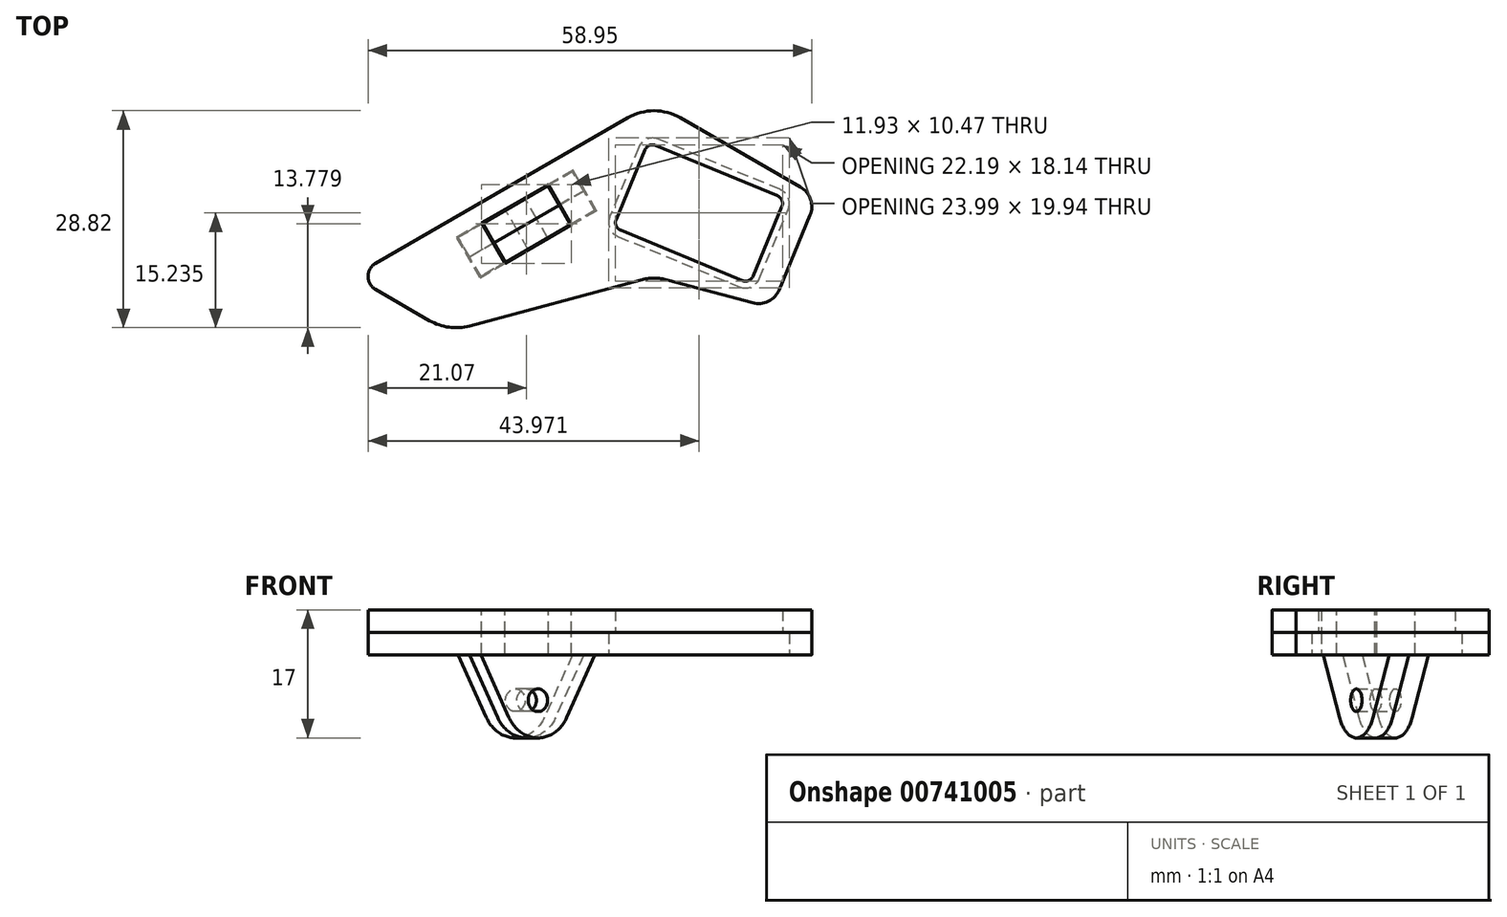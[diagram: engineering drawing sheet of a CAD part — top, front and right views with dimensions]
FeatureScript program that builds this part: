
annotation { "Feature Type Name" : "Feature", "Feature Type Description" : "" }
export const myFeature = defineFeature(function(context is Context, id is Id, definition is map)
    precondition{}
    {
        {
            var Q0;
            Q0=qCreatedBy(makeId("Top.planeOp"),FACE);
            var sketch = newSketch(context, id + "F0", { "sketchPlane" : qUnion([Q0])});
            skLineSegment(sketch, "E0", {"start": v(-37, 1.73) * mm, "end": v(-3.5, 21.07) * mm});
            skLineSegment(sketch, "E1", {"start": v(40, 0) * mm, "end": v(21.73, 10.55) * mm, "construction": true});
            skLineSegment(sketch, "E2", {"start": v(-1.81, -0.49) * mm, "end": v(-24.52, -6.57) * mm});
            skLineSegment(sketch, "E3", {"start": v(0, 0) * mm, "end": v(0, 23.1) * mm, "construction": true});
            skLineSegment(sketch, "E4", {"start": v(40, 0) * mm, "end": v(27.32, -7.32) * mm, "construction": true});
            skLineSegment(sketch, "E5", {"start": v(-29.83, -5.87) * mm, "end": v(-40, 0) * mm});
            skLineSegment(sketch, "E6", {"start": v(27.32, -7.32) * mm, "end": v(0, -23.1) * mm, "construction": true});
            skLineSegment(sketch, "E7", {"start": v(0, -23.1) * mm, "end": v(-37, -1.73) * mm, "construction": true});
            skLineSegment(sketch, "E8", {"start": v(13.99, -0.3) * mm, "end": v(17.82, 8.93) * mm});
            skLineSegment(sketch, "E9", {"start": v(16.73, 11.54) * mm, "end": v(0.57, 18.24) * mm});
            skLineSegment(sketch, "E10", {"start": v(-2.05, 17.16) * mm, "end": v(-5.87, 7.92) * mm});
            skLineSegment(sketch, "E11", {"start": v(-4.8, 5.3) * mm, "end": v(11.38, -1.4) * mm});
            skPoint(sketch, "E12.visualSharp", {"position": v(-6.64, 6.07) * mm});
            skArc(sketch, "E12.filletArc", {"start": v(-5.87, 7.92) * mm, "mid": v(-5.87, 6.39) * mm, "end": v(-4.8, 5.3) * mm});
            skPoint(sketch, "E13.visualSharp", {"position": v(-1.28, 19) * mm});
            skArc(sketch, "E13.filletArc", {"start": v(0.57, 18.24) * mm, "mid": v(-0.96, 18.24) * mm, "end": v(-2.05, 17.16) * mm});
            skPoint(sketch, "E14.visualSharp", {"position": v(18.58, 10.78) * mm});
            skArc(sketch, "E14.filletArc", {"start": v(17.82, 8.93) * mm, "mid": v(17.82, 10.46) * mm, "end": v(16.73, 11.54) * mm});
            skPoint(sketch, "E15.visualSharp", {"position": v(13.22, -2.16) * mm});
            skArc(sketch, "E15.filletArc", {"start": v(11.38, -1.4) * mm, "mid": v(12.9, -1.4) * mm, "end": v(13.99, -0.3) * mm});
            skLineSegment(sketch, "E16", {"start": v(16.64, -1.76) * mm, "end": v(20.73, 8.12) * mm});
            skLineSegment(sketch, "E17", {"start": v(15.63, -4.19) * mm, "end": v(27.32, -7.32) * mm, "construction": true});
            skLineSegment(sketch, "E18", {"start": v(13.09, -3.5) * mm, "end": v(1.81, -0.49) * mm});
            skLineSegment(sketch, "E19", {"start": v(3.5, 21.07) * mm, "end": v(19.45, 11.86) * mm});
            skPoint(sketch, "E20.visualSharp", {"position": v(15.63, -4.19) * mm});
            skArc(sketch, "E20.filletArc", {"start": v(13.09, -3.5) * mm, "mid": v(15.2, -3.3) * mm, "end": v(16.64, -1.76) * mm});
            skPoint(sketch, "E21.visualSharp", {"position": v(21.73, 10.55) * mm});
            skArc(sketch, "E21.filletArc", {"start": v(20.73, 8.12) * mm, "mid": v(20.8, 10.23) * mm, "end": v(19.45, 11.86) * mm});
            skPoint(sketch, "E22.visualSharp", {"position": v(0, 0) * mm});
            skArc(sketch, "E22.filletArc", {"start": v(1.81, -0.49) * mm, "mid": v(0, -0.25) * mm, "end": v(-1.81, -0.49) * mm});
            skPoint(sketch, "E23.visualSharp", {"position": v(-27.32, -7.32) * mm});
            skArc(sketch, "E23.filletArc", {"start": v(-29.83, -5.87) * mm, "mid": v(-27.25, -6.75) * mm, "end": v(-24.52, -6.57) * mm});
            skPoint(sketch, "E24.visualSharp", {"position": v(0, 23.1) * mm});
            skArc(sketch, "E24.filletArc", {"start": v(3.5, 21.07) * mm, "mid": v(0, 22.01) * mm, "end": v(-3.5, 21.07) * mm});
            skPoint(sketch, "E25.visualSharp", {"position": v(-40, 0) * mm});
            skArc(sketch, "E25.filletArc", {"start": v(-37, 1.73) * mm, "mid": v(-38, 0) * mm, "end": v(-37, -1.73) * mm});
            skSolve(sketch);
        }
        {
            var Q0;
            Q0=makeQuery(id+"F0.imprint","IMPRINT",FACE,{"disambiguationData":[TD([[makeQuery(id+"F0.imprint","IMPRINT",EDGE,{"derivedFrom":sQuery(id+"F0.wireOp",EDGE,"E0")}),-1.0]])]});
            extrude(context, id + "F1", {"entities" : qUnion([Q0]), "depth" : 3 * mm, "offsetDistance" : 25 * mm});
        }
        {
            var Q0;
            Q0=makeQuery(id+"F1.opExtrude","CAP_FACE",FACE,{"disambiguationData":[OSD([sQuery(id+"F0.wireOp",EDGE,"E0"),sQuery(id+"F0.wireOp",EDGE,"E2"),sQuery(id+"F0.wireOp",EDGE,"E5"),sQuery(id+"F0.wireOp",EDGE,"E8"),sQuery(id+"F0.wireOp",EDGE,"E9"),sQuery(id+"F0.wireOp",EDGE,"E10"),sQuery(id+"F0.wireOp",EDGE,"E11"),sQuery(id+"F0.wireOp",EDGE,"E12.filletArc"),sQuery(id+"F0.wireOp",EDGE,"E13.filletArc"),sQuery(id+"F0.wireOp",EDGE,"E14.filletArc"),sQuery(id+"F0.wireOp",EDGE,"E15.filletArc"),sQuery(id+"F0.wireOp",EDGE,"E16"),sQuery(id+"F0.wireOp",EDGE,"E18"),sQuery(id+"F0.wireOp",EDGE,"E19"),sQuery(id+"F0.wireOp",EDGE,"E20.filletArc"),sQuery(id+"F0.wireOp",EDGE,"E21.filletArc"),sQuery(id+"F0.wireOp",EDGE,"E22.filletArc"),sQuery(id+"F0.wireOp",EDGE,"E23.filletArc"),sQuery(id+"F0.wireOp",EDGE,"E24.filletArc"),sQuery(id+"F0.wireOp",EDGE,"E25.filletArc")])],"isStart":false});
            var sketch = newSketch(context, id + "F2", { "sketchPlane" : qUnion([Q0])});
            skArc(sketch, "E26.0", {"start": v(-5.04, 7.58) * mm, "mid": v(-5.04, 6.73) * mm, "end": v(-4.45, 6.14) * mm});
            skLineSegment(sketch, "E26.1", {"start": v(-1.22, 16.81) * mm, "end": v(-5.04, 7.58) * mm});
            skLineSegment(sketch, "E26.2", {"start": v(-4.45, 6.14) * mm, "end": v(11.72, -0.56) * mm});
            skArc(sketch, "E26.3", {"start": v(0.22, 17.4) * mm, "mid": v(-0.62, 17.4) * mm, "end": v(-1.22, 16.81) * mm});
            skArc(sketch, "E26.4", {"start": v(11.72, -0.56) * mm, "mid": v(12.56, -0.56) * mm, "end": v(13.16, 0.04) * mm});
            skLineSegment(sketch, "E26.5", {"start": v(13.16, 0.04) * mm, "end": v(16.98, 9.28) * mm});
            skArc(sketch, "E26.6", {"start": v(16.98, 9.28) * mm, "mid": v(16.98, 10.12) * mm, "end": v(16.39, 10.71) * mm});
            skLineSegment(sketch, "E26.7", {"start": v(16.39, 10.71) * mm, "end": v(0.22, 17.4) * mm});
            skLineSegment(sketch, "E27.0", {"start": v(13.09, -3.5) * mm, "end": v(1.81, -0.49) * mm});
            skArc(sketch, "E28.0", {"start": v(13.09, -3.5) * mm, "mid": v(15.2, -3.3) * mm, "end": v(16.64, -1.76) * mm});
            skLineSegment(sketch, "E29.0", {"start": v(16.64, -1.76) * mm, "end": v(20.73, 8.12) * mm});
            skArc(sketch, "E30.0", {"start": v(20.73, 8.12) * mm, "mid": v(20.8, 10.23) * mm, "end": v(19.45, 11.86) * mm});
            skLineSegment(sketch, "E31.0", {"start": v(3.5, 21.07) * mm, "end": v(19.45, 11.86) * mm});
            skArc(sketch, "E32.0", {"start": v(3.5, 21.07) * mm, "mid": v(0, 22.01) * mm, "end": v(-3.5, 21.07) * mm});
            skLineSegment(sketch, "E33.0", {"start": v(-37, 1.73) * mm, "end": v(-3.5, 21.07) * mm});
            skArc(sketch, "E34.0", {"start": v(-37, 1.73) * mm, "mid": v(-38, 0) * mm, "end": v(-37, -1.73) * mm});
            skLineSegment(sketch, "E35.0", {"start": v(-29.83, -5.87) * mm, "end": v(-37, -1.73) * mm});
            skArc(sketch, "E36.0", {"start": v(-29.83, -5.87) * mm, "mid": v(-27.25, -6.75) * mm, "end": v(-24.52, -6.57) * mm});
            skLineSegment(sketch, "E37.0", {"start": v(-1.81, -0.49) * mm, "end": v(-24.52, -6.57) * mm});
            skArc(sketch, "E38.0", {"start": v(1.81, -0.49) * mm, "mid": v(0, -0.25) * mm, "end": v(-1.81, -0.49) * mm});
            skSolve(sketch);
        }
        {
            var Q0;
            Q0=qSketchRegion(id+"F2",true);
            extrude(context, id + "F3", {"entities" : qUnion([Q0]), "depth" : 3 * mm, "offsetDistance" : 25 * mm});
        }
        {
            var Q0;
            Q0=makeQuery(id+"F1.opExtrude","CAP_FACE",FACE,{"disambiguationData":[OSD([sQuery(id+"F0.wireOp",EDGE,"E0"),sQuery(id+"F0.wireOp",EDGE,"E2"),sQuery(id+"F0.wireOp",EDGE,"E5"),sQuery(id+"F0.wireOp",EDGE,"E8"),sQuery(id+"F0.wireOp",EDGE,"E9"),sQuery(id+"F0.wireOp",EDGE,"E10"),sQuery(id+"F0.wireOp",EDGE,"E11"),sQuery(id+"F0.wireOp",EDGE,"E12.filletArc"),sQuery(id+"F0.wireOp",EDGE,"E13.filletArc"),sQuery(id+"F0.wireOp",EDGE,"E14.filletArc"),sQuery(id+"F0.wireOp",EDGE,"E15.filletArc"),sQuery(id+"F0.wireOp",EDGE,"E16"),sQuery(id+"F0.wireOp",EDGE,"E18"),sQuery(id+"F0.wireOp",EDGE,"E19"),sQuery(id+"F0.wireOp",EDGE,"E20.filletArc"),sQuery(id+"F0.wireOp",EDGE,"E21.filletArc"),sQuery(id+"F0.wireOp",EDGE,"E22.filletArc"),sQuery(id+"F0.wireOp",EDGE,"E23.filletArc"),sQuery(id+"F0.wireOp",EDGE,"E24.filletArc"),sQuery(id+"F0.wireOp",EDGE,"E25.filletArc")])],"isStart":true});
            var sketch = newSketch(context, id + "F4", { "sketchPlane" : qUnion([Q0])});
            skLineSegment(sketch, "E39.0", {"start": v(-29.83, 5.87) * mm, "end": v(-37, 1.73) * mm});
            skArc(sketch, "E40.0", {"start": v(-29.83, 5.87) * mm, "mid": v(-27.25, 6.75) * mm, "end": v(-24.52, 6.57) * mm});
            skArc(sketch, "E41.0", {"start": v(-37, -1.73) * mm, "mid": v(-38, 0) * mm, "end": v(-37, 1.73) * mm});
            skLineSegment(sketch, "E42.0", {"start": v(-1.81, 0.49) * mm, "end": v(-24.52, 6.57) * mm});
            skLineSegment(sketch, "E43.0", {"start": v(-37, -1.73) * mm, "end": v(-24.97, -8.68) * mm});
            skLineSegment(sketch, "E44", {"start": v(-24.97, -8.68) * mm, "end": v(-17.31, -2.25) * mm});
            skLineSegment(sketch, "E45", {"start": v(-17.31, -2.25) * mm, "end": v(-1.81, 0.49) * mm});
            skPoint(sketch, "E46.orphan", {"position": v(-3.5, -21.07) * mm});
            skSolve(sketch);
        }
        {
            var Q0;
            Q0=makeQuery(id+"F1.opExtrude","SWEPT_FACE",FACE,{"disambiguationData":[OSD([sQuery(id+"F0.wireOp",EDGE,"E0")])]});
            cPlane(context, id + "F5", {"entities" : qUnion([Q0]), "cplaneType" : CPlaneType.OFFSET, "offset" : 2.5 * mm, "oppositeDirection" : true, "width" : 150 * mm, "height" : 150 * mm});
        }
        {
            var Q0;
            Q0=qCreatedBy(id+"F5.planeOp",FACE);
            var sketch = newSketch(context, id + "F6", { "sketchPlane" : qUnion([Q0])});
            skCircle(sketch, "E47", {"center": v(11.18, -6) * mm, "radius": 1.5 * mm});
            skCircle(sketch, "E48", {"center": v(11.18, -6) * mm, "radius": 5 * mm});
            skLineSegment(sketch, "E49", {"start": v(15.61, -8.3) * mm, "end": v(19.94, 0) * mm});
            skLineSegment(sketch, "E50", {"start": v(19.94, 0) * mm, "end": v(2.42, 0) * mm});
            skLineSegment(sketch, "E51", {"start": v(2.42, 0) * mm, "end": v(6.74, -8.3) * mm});
            skLineSegment(sketch, "E52.bottom", {"start": v(6.18, 0) * mm, "end": v(16.18, 0) * mm});
            skLineSegment(sketch, "E52.top", {"start": v(6.18, 6) * mm, "end": v(16.18, 6) * mm});
            skLineSegment(sketch, "E52.left", {"start": v(6.18, 0) * mm, "end": v(6.18, 6) * mm});
            skLineSegment(sketch, "E52.right", {"start": v(16.18, 0) * mm, "end": v(16.18, 6) * mm});
            skPoint(sketch, "E52.middle", {"position": v(11.18, 3) * mm});
            skPoint(sketch, "E52.middle.positionSnap0", {"position": v(11.18, 0) * mm});
            skPoint(sketch, "E52.centerSnap0", {"position": v(11.18, 0) * mm});
            skSolve(sketch);
        }
        {
            var Q0;
            Q0=qSketchRegion(id+"F6",true);
            extrude(context, id + "F7", {"entities" : qUnion([Q0]), "oppositeDirection" : true, "depth" : 3 * mm, "offsetDistance" : 25 * mm});
        }
        {
            var Q0;
            Q0=makeQuery(id+"F7.opExtrude","SWEPT_BODY",BODY,{"disambiguationData":[OSD([sQuery(id+"F6.wireOp",EDGE,"E47"),sQuery(id+"F6.wireOp",EDGE,"E48"),sQuery(id+"F6.wireOp",EDGE,"E49"),sQuery(id+"F6.wireOp",EDGE,"E50"),sQuery(id+"F6.wireOp",EDGE,"E51"),sQuery(id+"F6.wireOp",EDGE,"E52.top"),sQuery(id+"F6.wireOp",EDGE,"E52.left"),sQuery(id+"F6.wireOp",EDGE,"E52.right")])]});
            var Q1;
            Q1=makeQuery(id+"F7.opExtrude","SWEPT_EDGE",EDGE,{"disambiguationData":[OSD([sQuery(id+"F6.wireOp",EDGE,"E48"),sQuery(id+"F6.wireOp",EDGE,"E51")])]});
            transform(context, id + "F8", {"entities" : qUnion([Q0]), "transformType" : TransformType.TRANSLATION_ENTITY, "oppositeDirectionEntity" : true, "transformLine" : qUnion([Q1]), "makeCopy" : true});
        }
        {
            var Q0;
            Q0=makeQuery(id+"F8.opPattern","COPY",BODY,{"derivedFrom":makeQuery(id+"F7.opExtrude","SWEPT_BODY",BODY,{"disambiguationData":[OSD([sQuery(id+"F6.wireOp",EDGE,"E47"),sQuery(id+"F6.wireOp",EDGE,"E48"),sQuery(id+"F6.wireOp",EDGE,"E49"),sQuery(id+"F6.wireOp",EDGE,"E50"),sQuery(id+"F6.wireOp",EDGE,"E51"),sQuery(id+"F6.wireOp",EDGE,"E52.top"),sQuery(id+"F6.wireOp",EDGE,"E52.left"),sQuery(id+"F6.wireOp",EDGE,"E52.right")])]}),"instanceName":"1"});
            var Q1;
            Q1=makeQuery(id+"F7.opExtrude","SWEPT_BODY",BODY,{"disambiguationData":[OSD([sQuery(id+"F6.wireOp",EDGE,"E47"),sQuery(id+"F6.wireOp",EDGE,"E48"),sQuery(id+"F6.wireOp",EDGE,"E49"),sQuery(id+"F6.wireOp",EDGE,"E50"),sQuery(id+"F6.wireOp",EDGE,"E51"),sQuery(id+"F6.wireOp",EDGE,"E52.top"),sQuery(id+"F6.wireOp",EDGE,"E52.left"),sQuery(id+"F6.wireOp",EDGE,"E52.right")])]});
            var Q2;
            Q2=makeQuery(id+"F1.opExtrude","SWEPT_BODY",BODY,{"disambiguationData":[OSD([sQuery(id+"F0.wireOp",EDGE,"E0"),sQuery(id+"F0.wireOp",EDGE,"E2"),sQuery(id+"F0.wireOp",EDGE,"E5"),sQuery(id+"F0.wireOp",EDGE,"E8"),sQuery(id+"F0.wireOp",EDGE,"E9"),sQuery(id+"F0.wireOp",EDGE,"E10"),sQuery(id+"F0.wireOp",EDGE,"E11"),sQuery(id+"F0.wireOp",EDGE,"E12.filletArc"),sQuery(id+"F0.wireOp",EDGE,"E13.filletArc"),sQuery(id+"F0.wireOp",EDGE,"E14.filletArc"),sQuery(id+"F0.wireOp",EDGE,"E15.filletArc"),sQuery(id+"F0.wireOp",EDGE,"E16"),sQuery(id+"F0.wireOp",EDGE,"E18"),sQuery(id+"F0.wireOp",EDGE,"E19"),sQuery(id+"F0.wireOp",EDGE,"E20.filletArc"),sQuery(id+"F0.wireOp",EDGE,"E21.filletArc"),sQuery(id+"F0.wireOp",EDGE,"E22.filletArc"),sQuery(id+"F0.wireOp",EDGE,"E23.filletArc"),sQuery(id+"F0.wireOp",EDGE,"E24.filletArc"),sQuery(id+"F0.wireOp",EDGE,"E25.filletArc")])]});
            var Q3;
            Q3=makeQuery(id+"F3.opExtrude","SWEPT_BODY",BODY,{"disambiguationData":[OSD([sQuery(id+"F2.wireOp",EDGE,"E26.0"),sQuery(id+"F2.wireOp",EDGE,"E26.1"),sQuery(id+"F2.wireOp",EDGE,"E26.2"),sQuery(id+"F2.wireOp",EDGE,"E26.3"),sQuery(id+"F2.wireOp",EDGE,"E26.4"),sQuery(id+"F2.wireOp",EDGE,"E26.5"),sQuery(id+"F2.wireOp",EDGE,"E26.6"),sQuery(id+"F2.wireOp",EDGE,"E26.7"),sQuery(id+"F2.wireOp",EDGE,"E27.0"),sQuery(id+"F2.wireOp",EDGE,"E28.0"),sQuery(id+"F2.wireOp",EDGE,"E29.0"),sQuery(id+"F2.wireOp",EDGE,"E30.0"),sQuery(id+"F2.wireOp",EDGE,"E31.0"),sQuery(id+"F2.wireOp",EDGE,"E32.0"),sQuery(id+"F2.wireOp",EDGE,"E33.0"),sQuery(id+"F2.wireOp",EDGE,"E34.0"),sQuery(id+"F2.wireOp",EDGE,"E35.0"),sQuery(id+"F2.wireOp",EDGE,"E36.0"),sQuery(id+"F2.wireOp",EDGE,"E37.0"),sQuery(id+"F2.wireOp",EDGE,"E38.0")])]});
            booleanBodies(context, id + "F9", {"operationType" : BooleanOperationType.SUBTRACTION, "tools" : qUnion([Q0, Q1]), "targets" : qUnion([Q2, Q3]), "offset" : true, "offsetAll" : true, "offsetDistance" : .1 * mm, "keepTools" : true});
        }
    });
